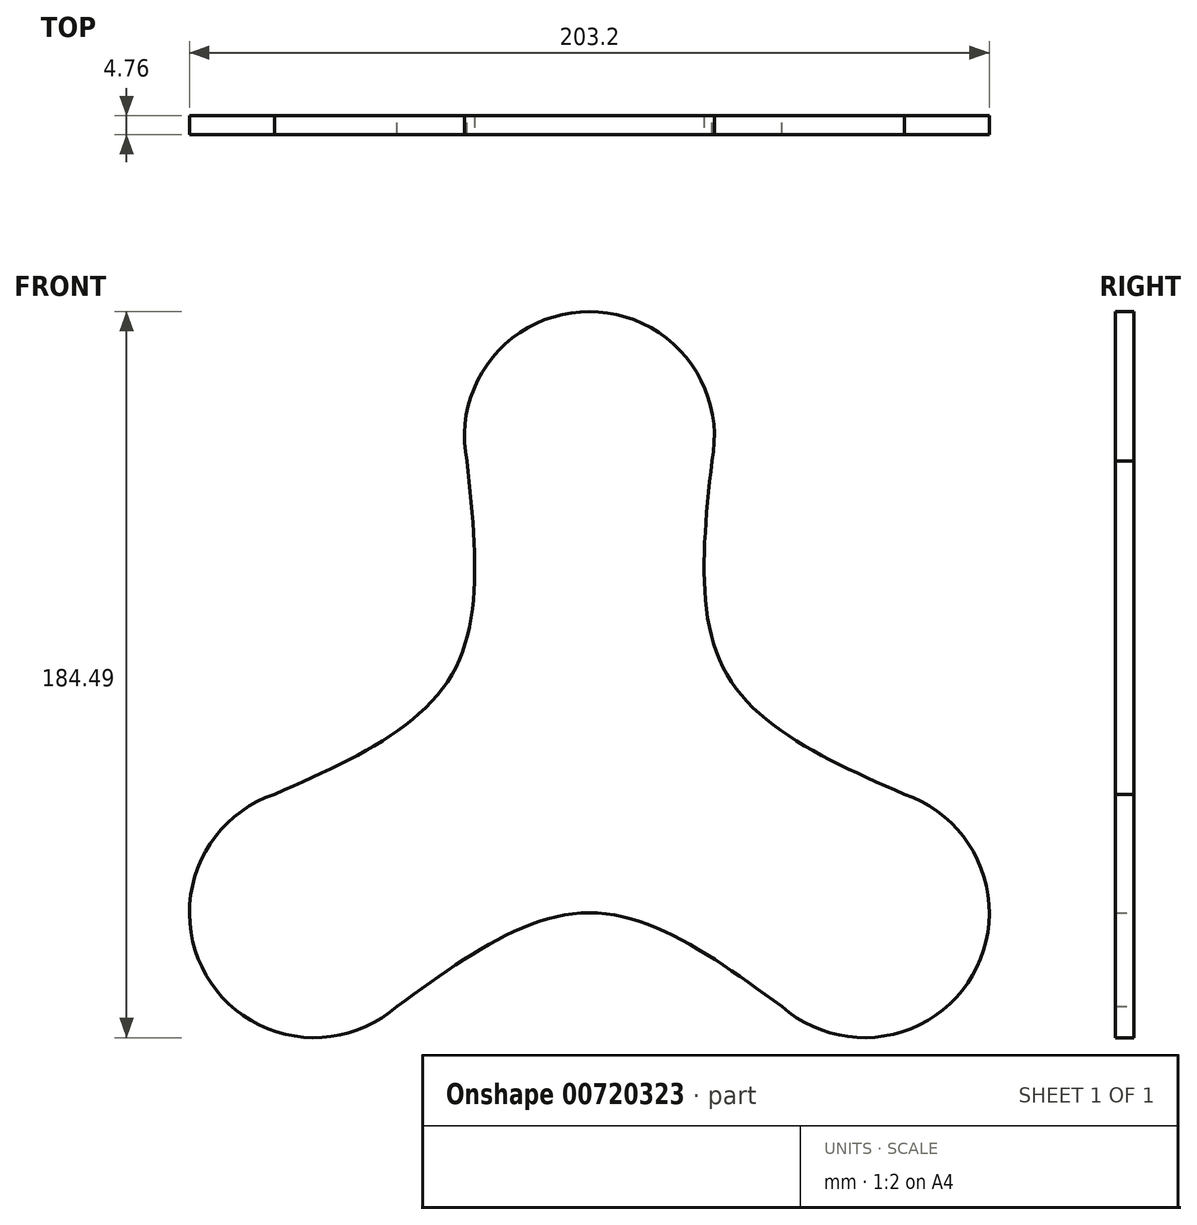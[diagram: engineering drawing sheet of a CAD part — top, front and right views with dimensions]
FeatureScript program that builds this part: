
annotation { "Feature Type Name" : "Feature", "Feature Type Description" : "" }
export const myFeature = defineFeature(function(context is Context, id is Id, definition is map)
    precondition{}
    {
        {
            var Q0;
            Q0=qCreatedBy(makeId("Front.planeOp"),FACE);
            var sketch = newSketch(context, id + "F0", { "sketchPlane" : qUnion([Q0])});
            skCircle(sketch, "E0.cCircle", {"center": v(0, 0) * mm, "radius": 161.31 * mm, "construction": true});
            skLineSegment(sketch, "E0.0", {"start": v(139.7, -80.66) * mm, "end": v(-139.7, -80.66) * mm});
            skLineSegment(sketch, "E0.1", {"start": v(-139.7, -80.66) * mm, "end": v(0, 161.31) * mm});
            skLineSegment(sketch, "E0.2", {"start": v(0, 161.31) * mm, "end": v(139.7, -80.66) * mm});
            skCircle(sketch, "E1", {"center": v(-139.7, -80.66) * mm, "radius": 63.5 * mm});
            skCircle(sketch, "E2", {"center": v(0, 161.31) * mm, "radius": 63.5 * mm});
            skCircle(sketch, "E3", {"center": v(139.7, -80.66) * mm, "radius": 63.5 * mm});
            skArc(sketch, "E4", {"start": v(-160.01, -20.5) * mm, "mid": v(-139.7, -80.66) * mm, "end": v(-97.75, -128.33) * mm});
            skFitSpline(sketch, "E5", {"points": [v(-160.01, -20.5) * mm, v(-69.85, 40.33) * mm, v(-62.26, 148.82) * mm], "startDerivative": vector(221.6, 97.8) * mm, "endDerivative": vector(-26.1, 240.82) * mm});
            skFitSpline(sketch, "E6", {"points": [v(-97.75, -128.33) * mm, v(0, -80.66) * mm, v(97.75, -128.33) * mm], "startDerivative": vector(195.5, 143.02) * mm, "endDerivative": vector(195.5, -143.02) * mm});
            skFitSpline(sketch, "E7", {"points": [v(62.26, 148.82) * mm, v(69.85, 40.33) * mm, v(160.01, -20.5) * mm], "startDerivative": vector(-26.1, -240.82) * mm, "endDerivative": vector(221.6, -97.8) * mm});
            skArc(sketch, "E8.trimOffspring", {"start": v(62.26, 148.82) * mm, "mid": v(0, 161.32) * mm, "end": v(-62.26, 148.82) * mm});
            skArc(sketch, "E9.trimOffspring", {"start": v(97.75, -128.33) * mm, "mid": v(139.7, -80.66) * mm, "end": v(160.01, -20.5) * mm});
            skSolve(sketch);
        }
        {
            var Q0;
            {var subQ0=sQuery(id+"F0.wireOp",EDGE,"E8.trimOffspring");Q0=makeQuery(id+"F0.imprint","IMPRINT",FACE,{"disambiguationData":[TD([[makeQuery(id+"F0.imprint","IMPRINT",EDGE,{"derivedFrom":subQ0}),-1.0]])]});}
            var Q1;
            {var subQ0=sQuery(id+"F0.wireOp",EDGE,"E8.trimOffspring");Q1=makeQuery(id+"F0.imprint","IMPRINT",FACE,{"disambiguationData":[TD([[makeQuery(id+"F0.imprint","IMPRINT",EDGE,{"derivedFrom":subQ0}),1.0]])]});}
            var Q2;
            {var subQ4=sQuery(id+"F0.wireOp",EDGE,"E0.0");var subQ5=makeQuery(id+"F0.imprint","INTERSECT",VERTEX,{"derivedFrom":[subQ4,sQuery(id+"F0.wireOp",EDGE,"E6")]});Q2=makeQuery(id+"F0.imprint","IMPRINT",FACE,{"disambiguationData":[TD([[makeQuery(id+"F0.imprint","IMPRINT",EDGE,{"disambiguationData":[TD([[subQ5,1.0]])],"derivedFrom":subQ4}),-1.0]])]});}
            var Q3;
            {var subQ0=sQuery(id+"F0.wireOp",EDGE,"E7");var subQ1=sQuery(id+"F0.wireOp",EDGE,"E0.2");var subQ2=makeQuery(id+"F0.imprint","INTERSECT",VERTEX,{"derivedFrom":[subQ1,subQ0]});Q3=makeQuery(id+"F0.imprint","IMPRINT",FACE,{"disambiguationData":[TD([[makeQuery(id+"F0.imprint","IMPRINT",EDGE,{"disambiguationData":[TD([[subQ2,1.0]])],"derivedFrom":subQ1}),1.0]])]});}
            var Q4;
            {var subQ0=sQuery(id+"F0.wireOp",EDGE,"E5");var subQ1=sQuery(id+"F0.wireOp",EDGE,"E0.1");var subQ2=makeQuery(id+"F0.imprint","INTERSECT",VERTEX,{"derivedFrom":[subQ1,subQ0]});Q4=makeQuery(id+"F0.imprint","IMPRINT",FACE,{"disambiguationData":[TD([[makeQuery(id+"F0.imprint","IMPRINT",EDGE,{"disambiguationData":[TD([[subQ2,-1.0]])],"derivedFrom":subQ1}),1.0]])]});}
            var Q5;
            {var subQ0=sQuery(id+"F0.wireOp",EDGE,"E0.2");var subQ1=sQuery(id+"F0.wireOp",EDGE,"E0.1");var subQ2=makeQuery(id+"F0.imprint","INTERSECT",VERTEX,{"derivedFrom":[subQ1,subQ0]});Q5=makeQuery(id+"F0.imprint","IMPRINT",FACE,{"disambiguationData":[TD([[makeQuery(id+"F0.imprint","IMPRINT",EDGE,{"disambiguationData":[TD([[subQ2,1.0]])],"derivedFrom":subQ1}),-1.0]])]});}
            var Q6;
            {var subQ0=sQuery(id+"F0.wireOp",EDGE,"E9.trimOffspring");Q6=makeQuery(id+"F0.imprint","IMPRINT",FACE,{"disambiguationData":[TD([[makeQuery(id+"F0.imprint","IMPRINT",EDGE,{"derivedFrom":subQ0}),-1.0]])]});}
            var Q7;
            {var subQ0=sQuery(id+"F0.wireOp",EDGE,"E0.2");var subQ1=sQuery(id+"F0.wireOp",EDGE,"E0.0");var subQ2=makeQuery(id+"F0.imprint","INTERSECT",VERTEX,{"derivedFrom":[subQ1,subQ0]});Q7=makeQuery(id+"F0.imprint","IMPRINT",FACE,{"disambiguationData":[TD([[makeQuery(id+"F0.imprint","IMPRINT",EDGE,{"disambiguationData":[TD([[subQ2,-1.0]])],"derivedFrom":subQ1}),-1.0]])]});}
            var Q8;
            {var subQ0=sQuery(id+"F0.wireOp",EDGE,"E9.trimOffspring");Q8=makeQuery(id+"F0.imprint","IMPRINT",FACE,{"disambiguationData":[TD([[makeQuery(id+"F0.imprint","IMPRINT",EDGE,{"derivedFrom":subQ0}),1.0]])]});}
            var Q9;
            {var subQ0=sQuery(id+"F0.wireOp",EDGE,"E7");var subQ1=sQuery(id+"F0.wireOp",EDGE,"E0.2");var subQ2=makeQuery(id+"F0.imprint","INTERSECT",VERTEX,{"derivedFrom":[subQ1,subQ0]});Q9=makeQuery(id+"F0.imprint","IMPRINT",FACE,{"disambiguationData":[TD([[makeQuery(id+"F0.imprint","IMPRINT",EDGE,{"disambiguationData":[TD([[subQ2,-1.0]])],"derivedFrom":subQ1}),1.0]])]});}
            var Q10;
            {var subQ0=sQuery(id+"F0.wireOp",EDGE,"E6");var subQ1=sQuery(id+"F0.wireOp",EDGE,"E0.0");var subQ2=makeQuery(id+"F0.imprint","INTERSECT",VERTEX,{"derivedFrom":[subQ1,subQ0]});Q10=makeQuery(id+"F0.imprint","IMPRINT",FACE,{"disambiguationData":[TD([[makeQuery(id+"F0.imprint","IMPRINT",EDGE,{"disambiguationData":[TD([[subQ2,1.0]])],"derivedFrom":subQ1}),1.0]])]});}
            var Q11;
            {var subQ0=sQuery(id+"F0.wireOp",EDGE,"E6");var subQ1=sQuery(id+"F0.wireOp",EDGE,"E0.0");var subQ2=makeQuery(id+"F0.imprint","INTERSECT",VERTEX,{"derivedFrom":[subQ1,subQ0]});Q11=makeQuery(id+"F0.imprint","IMPRINT",FACE,{"disambiguationData":[TD([[makeQuery(id+"F0.imprint","IMPRINT",EDGE,{"disambiguationData":[TD([[subQ2,-1.0]])],"derivedFrom":subQ1}),1.0]])]});}
            var Q12;
            {var subQ0=sQuery(id+"F0.wireOp",EDGE,"E4");Q12=makeQuery(id+"F0.imprint","IMPRINT",FACE,{"disambiguationData":[TD([[makeQuery(id+"F0.imprint","IMPRINT",EDGE,{"derivedFrom":subQ0}),1.0]])]});}
            var Q13;
            {var subQ0=sQuery(id+"F0.wireOp",EDGE,"E0.1");var subQ1=sQuery(id+"F0.wireOp",EDGE,"E0.0");var subQ2=makeQuery(id+"F0.imprint","INTERSECT",VERTEX,{"derivedFrom":[subQ1,subQ0]});Q13=makeQuery(id+"F0.imprint","IMPRINT",FACE,{"disambiguationData":[TD([[makeQuery(id+"F0.imprint","IMPRINT",EDGE,{"disambiguationData":[TD([[subQ2,1.0]])],"derivedFrom":subQ1}),-1.0]])]});}
            var Q14;
            {var subQ0=sQuery(id+"F0.wireOp",EDGE,"E4");Q14=makeQuery(id+"F0.imprint","IMPRINT",FACE,{"disambiguationData":[TD([[makeQuery(id+"F0.imprint","IMPRINT",EDGE,{"derivedFrom":subQ0}),-1.0]])]});}
            var Q15;
            {var subQ0=sQuery(id+"F0.wireOp",EDGE,"E5");var subQ1=sQuery(id+"F0.wireOp",EDGE,"E0.1");var subQ2=makeQuery(id+"F0.imprint","INTERSECT",VERTEX,{"derivedFrom":[subQ1,subQ0]});Q15=makeQuery(id+"F0.imprint","IMPRINT",FACE,{"disambiguationData":[TD([[makeQuery(id+"F0.imprint","IMPRINT",EDGE,{"disambiguationData":[TD([[subQ2,1.0]])],"derivedFrom":subQ1}),1.0]])]});}
            extrude(context, id + "F1", {"entities" : qUnion([Q0, Q1, Q2, Q3, Q4, Q5, Q6, Q7, Q8, Q9, Q10, Q11, Q12, Q13, Q14, Q15]), "endBound" : BoundingType.SYMMETRIC, "depth" : 9.52 * mm, "offsetDistance" : 25.4 * mm});
        }
        {
            var Q0;
            Q0=makeQuery(id+"F1.opExtrude","SWEPT_BODY",BODY,{"disambiguationData":[OSD([sQuery(id+"F0.wireOp",EDGE,"E1"),sQuery(id+"F0.wireOp",EDGE,"E2"),sQuery(id+"F0.wireOp",EDGE,"E3"),sQuery(id+"F0.wireOp",EDGE,"E5"),sQuery(id+"F0.wireOp",EDGE,"E6"),sQuery(id+"F0.wireOp",EDGE,"E7")])]});
            var Q1;
            Q1=qCreatedBy(makeId("Origin.pointOp"),VERTEX);
            transform(context, id + "F2", {"entities" : qUnion([Q0]), "transformType" : TransformType.SCALE_UNIFORMLY, "scale" : .5, "scalePoint" : qUnion([Q1]), "makeCopy" : false});
        }
    });
